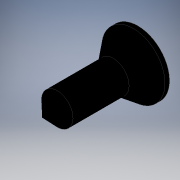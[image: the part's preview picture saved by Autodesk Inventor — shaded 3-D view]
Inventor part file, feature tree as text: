
AUTODESK INVENTOR PART (.ipt)
format: ipt  version: 2019 (Build 230136000, 136)  size: 133,632 bytes
history: native  units: mm
features: other x7, sketch x2, revolve x1, extrude x1
ambient origin geometry x8: Origin, YZ Plane, XZ Plane, XY Plane, X Axis, Y Axis, Z Axis, Center Point
bodies: Solid1 (feature_tree)
feature tree (11):
  revolve  "Revolution1"  [1 undecoded]
  extrude  "Extrusion1"  [1 undecoded]
  other  "CS_ANBAU_XY"
  other  "CS_ANBAU_YZ"
  other  "CS_ANBAU_ZX"
  other  "CS_ANBAU_X"
  other  "CS_ANBAU_Y"
  other  "CS_ANBAU_Z"
  other  "CS_ANBAU_Center"
  sketch  "Sketch_1"  dims[d0=360.0deg d1=2.0mm d2=0.0mm]
  sketch  "Sketch_3"  dims[d3=0.0mm]
note: 2 required parameter values undecoded (feature->parameter linkage not recoverable at this tier; creation-order binding heuristic only, values carry confidence <= 0.55)